# Revit family: EKF_EE_ВертикальнаяПередняяПанельTrivia_AVERES
name_source: partatom
category: Электрооборудование
units: mm (PartAtom-declared; Revit-internal decimal feet)

## family parameters
Всегда вертикально = Нет
На основе рабочей плоскости = Да
Общий = Да
При загрузке вырезать с полостями = Нет
Размер круглого соединителя = Использовать диаметр
Тип детали = Силовой щит
Точка расчета площади = Нет

## types (2) — shared parameters
ADSK_Единица измерения = шт.
ADSK_Завод-изготовитель = EKF
ADSK_Количество = 1
ADSK_Размер_Высота = 2000 мм
ADSK_Размер_Глубина = 35 мм
t2 = 1.5 мм
Вырез = 16 мм
Высота = 1915 мм
Глубина = 35 мм
Изготовитель = EKF
КрайниеКрепления = 37.5 мм
Отметка по умолчанию = 1219.2 мм
Серия номенклатуры = Averes
Степень защиты IP = -
ТВ = EKF_2_TRIVIA_AVERES
Тип установки = -
zero-valued in all types: ADSK_Масса

## per-type parameters (varying)
| type | ADSK_Код изделия | ADSK_Размер_Ширина | Тип | Ширина |
| Вертикальная передняя панель Ш200 В2000 EKF AVERES | FP2W200 | 200 мм | 641 мм | 175 мм |
| Вертикальная передняя панель Ш300 В2000 EKF AVERES | FP2W300 | 300 мм | 642 мм | 275 мм |

note: column(s) folded — value = type name in every type: ADSK_Марка, ADSK_Наименование, ADSK_Обозначение
